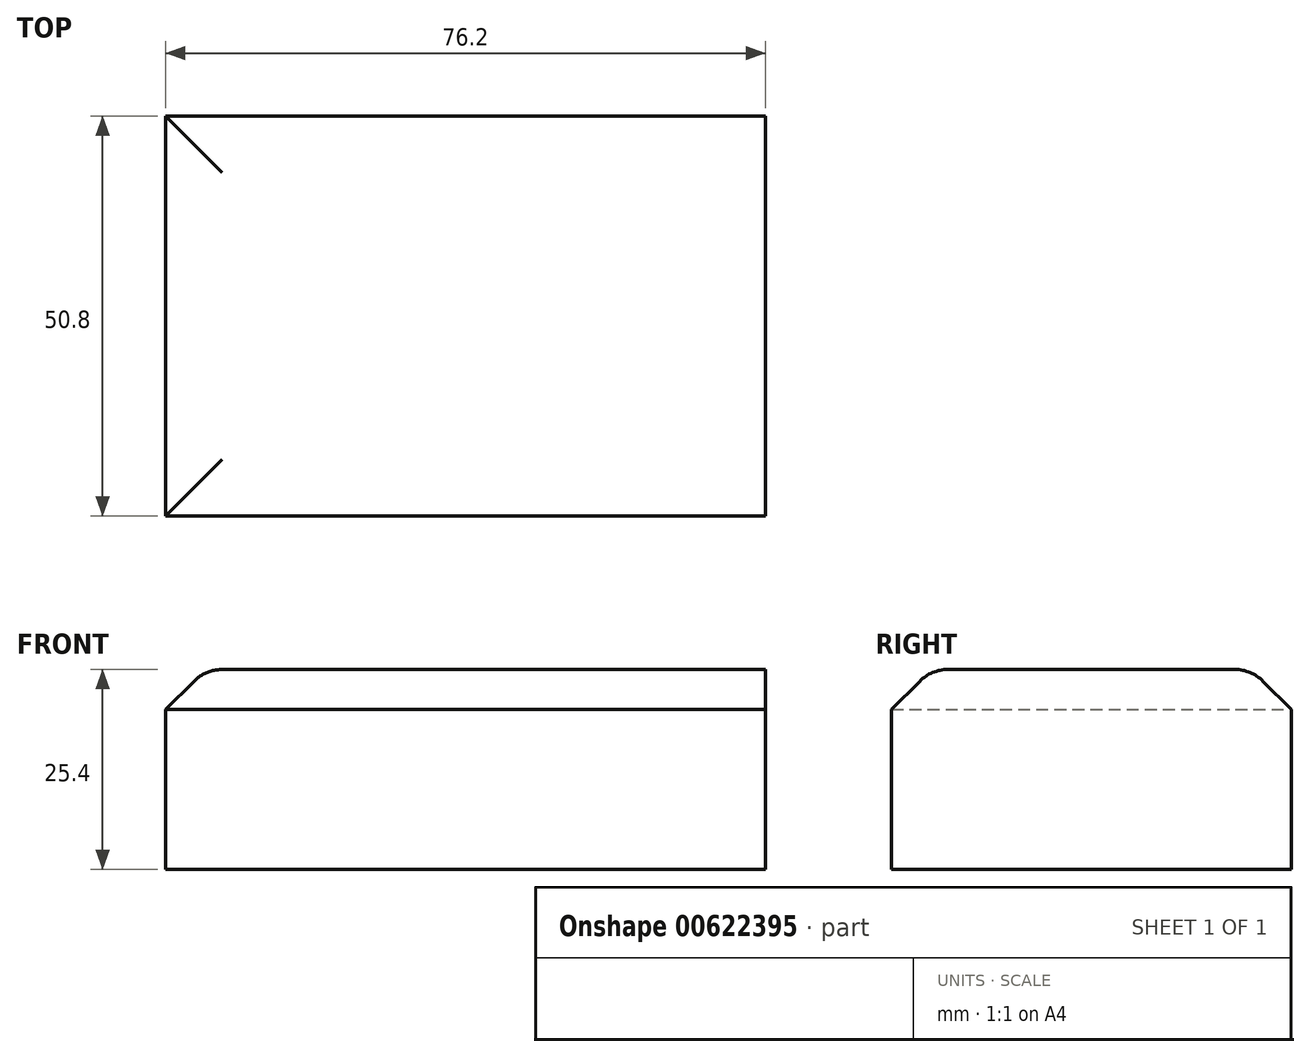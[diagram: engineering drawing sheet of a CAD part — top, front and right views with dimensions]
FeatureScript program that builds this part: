
annotation { "Feature Type Name" : "Feature", "Feature Type Description" : "" }
export const myFeature = defineFeature(function(context is Context, id is Id, definition is map)
    precondition{}
    {
        {
            var Q0;
            Q0=qCreatedBy(makeId("Top.planeOp"),FACE);
            var sketch = newSketch(context, id + "F0", { "sketchPlane" : qUnion([Q0])});
            skLineSegment(sketch, "E0.bottom", {"start": v(0, 0) * mm, "end": v(76.2, 0) * mm});
            skLineSegment(sketch, "E0.top", {"start": v(0, -50.8) * mm, "end": v(76.2, -50.8) * mm});
            skLineSegment(sketch, "E0.left", {"start": v(0, 0) * mm, "end": v(0, -50.8) * mm});
            skLineSegment(sketch, "E0.right", {"start": v(76.2, 0) * mm, "end": v(76.2, -50.8) * mm});
            skSolve(sketch);
        }
        {
            var Q0;
            Q0=makeQuery(id+"F0.imprint","IMPRINT",FACE,{"disambiguationData":[TD([[makeQuery(id+"F0.imprint","IMPRINT",EDGE,{"derivedFrom":sQuery(id+"F0.wireOp",EDGE,"E0.bottom")}),-1.0]])]});
            extrude(context, id + "F1", {"entities" : qUnion([Q0]), "depth" : 25.4 * mm, "offsetDistance" : 25.4 * mm});
        }
        {
            var Q0;
            Q0=makeQuery(id+"F1.opExtrude","CAP_EDGE",EDGE,{"disambiguationData":[OSD([sQuery(id+"F0.wireOp",EDGE,"E0.top")])],"isStart":false});
            var Q1;
            Q1=makeQuery(id+"F1.opExtrude","CAP_EDGE",EDGE,{"disambiguationData":[OSD([sQuery(id+"F0.wireOp",EDGE,"E0.left")])],"isStart":false});
            var Q2;
            Q2=makeQuery(id+"F1.opExtrude","CAP_EDGE",EDGE,{"disambiguationData":[OSD([sQuery(id+"F0.wireOp",EDGE,"E0.bottom")])],"isStart":false});
            chamfer(context, id + "F2", {"entities" : qUnion([Q0, Q1, Q2]), "width" : 5.08 * mm, "tangentPropagation" : true});
        }
        {
            var Q0;
            {var subQ0=sQuery(id+"F0.wireOp",EDGE,"E0.bottom");Q0=makeQuery(id+"F2.opChamfer","BLEND_EDGE",EDGE,{"blendedFrom":[makeQuery(id+"F1.opExtrude","CAP_EDGE",EDGE,{"disambiguationData":[OSD([subQ0])],"isStart":false}),makeQuery(id+"F1.opExtrude","CAP_FACE",FACE,{"disambiguationData":[OSD([subQ0,sQuery(id+"F0.wireOp",EDGE,"E0.top"),sQuery(id+"F0.wireOp",EDGE,"E0.left"),sQuery(id+"F0.wireOp",EDGE,"E0.right")])],"isStart":false})],"blendedInto":[makeQuery(id+"F1.opExtrude","CAP_FACE",FACE,{"disambiguationData":[OSD([subQ0,sQuery(id+"F0.wireOp",EDGE,"E0.top"),sQuery(id+"F0.wireOp",EDGE,"E0.left"),sQuery(id+"F0.wireOp",EDGE,"E0.right")])],"isStart":false})]});}
            var Q1;
            {var subQ0=sQuery(id+"F0.wireOp",EDGE,"E0.left");Q1=makeQuery(id+"F2.opChamfer","BLEND_EDGE",EDGE,{"blendedFrom":[makeQuery(id+"F1.opExtrude","CAP_EDGE",EDGE,{"disambiguationData":[OSD([subQ0])],"isStart":false}),makeQuery(id+"F1.opExtrude","CAP_FACE",FACE,{"disambiguationData":[OSD([sQuery(id+"F0.wireOp",EDGE,"E0.bottom"),sQuery(id+"F0.wireOp",EDGE,"E0.top"),subQ0,sQuery(id+"F0.wireOp",EDGE,"E0.right")])],"isStart":false})],"blendedInto":[makeQuery(id+"F1.opExtrude","CAP_FACE",FACE,{"disambiguationData":[OSD([sQuery(id+"F0.wireOp",EDGE,"E0.bottom"),sQuery(id+"F0.wireOp",EDGE,"E0.top"),subQ0,sQuery(id+"F0.wireOp",EDGE,"E0.right")])],"isStart":false})]});}
            var Q2;
            {var subQ0=sQuery(id+"F0.wireOp",EDGE,"E0.top");Q2=makeQuery(id+"F2.opChamfer","BLEND_EDGE",EDGE,{"blendedFrom":[makeQuery(id+"F1.opExtrude","CAP_EDGE",EDGE,{"disambiguationData":[OSD([subQ0])],"isStart":false}),makeQuery(id+"F1.opExtrude","CAP_FACE",FACE,{"disambiguationData":[OSD([sQuery(id+"F0.wireOp",EDGE,"E0.bottom"),subQ0,sQuery(id+"F0.wireOp",EDGE,"E0.left"),sQuery(id+"F0.wireOp",EDGE,"E0.right")])],"isStart":false})],"blendedInto":[makeQuery(id+"F1.opExtrude","CAP_FACE",FACE,{"disambiguationData":[OSD([sQuery(id+"F0.wireOp",EDGE,"E0.bottom"),subQ0,sQuery(id+"F0.wireOp",EDGE,"E0.left"),sQuery(id+"F0.wireOp",EDGE,"E0.right")])],"isStart":false})]});}
            fillet(context, id + "F3", {"entities" : qUnion([Q0, Q1, Q2]), "radius" : 5.08 * mm, "tangentPropagation" : true, "allowEdgeOverflow" : false});
        }
    });
